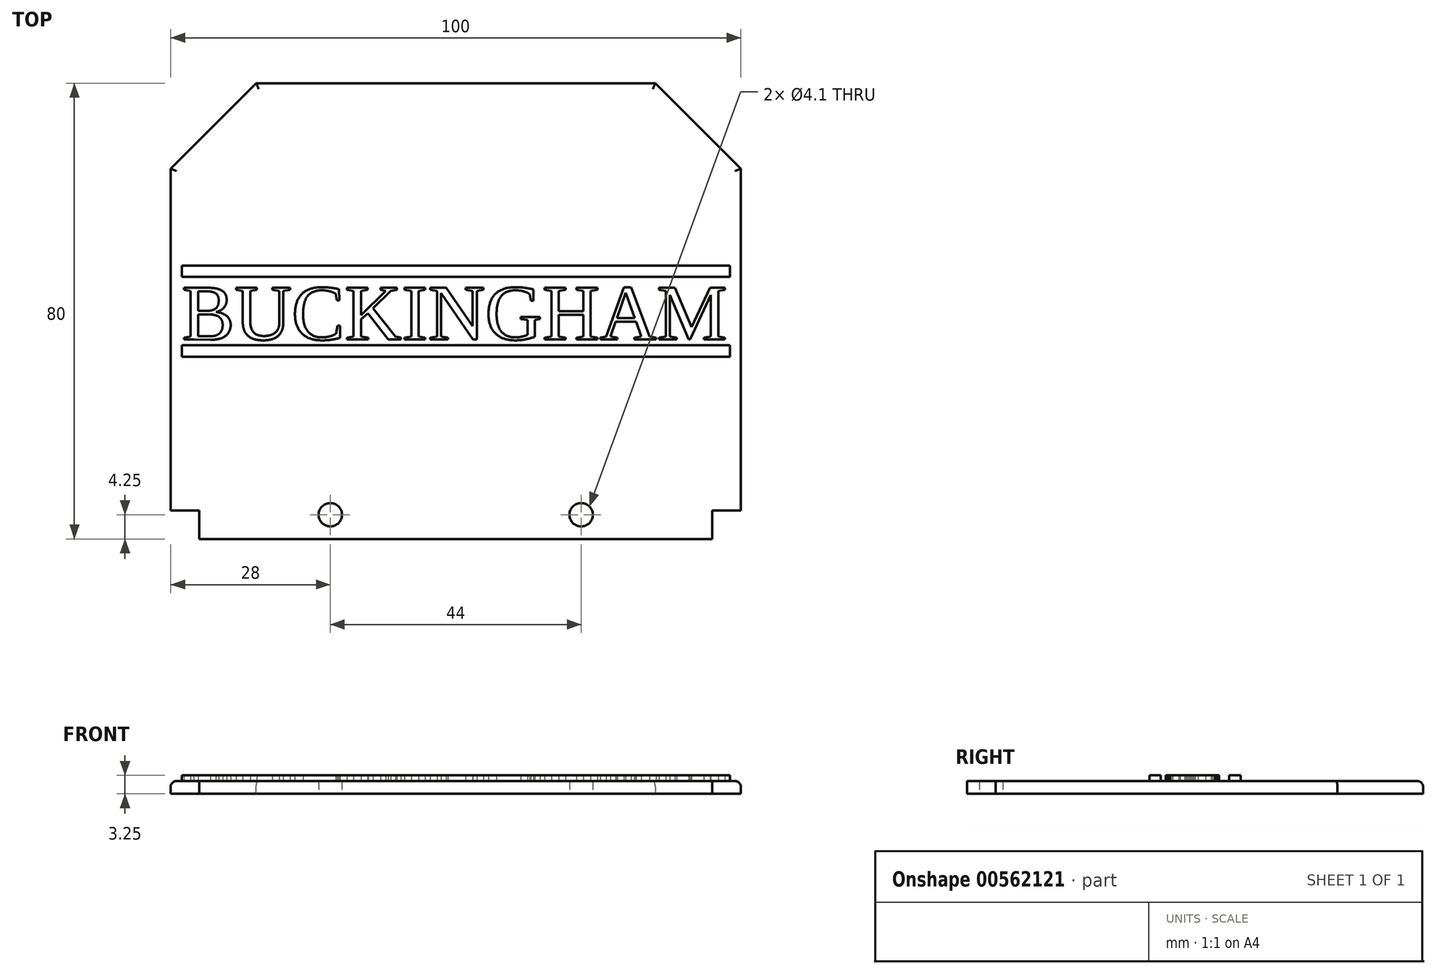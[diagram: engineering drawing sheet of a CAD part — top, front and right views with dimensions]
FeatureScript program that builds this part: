
annotation { "Feature Type Name" : "Feature", "Feature Type Description" : "" }
export const myFeature = defineFeature(function(context is Context, id is Id, definition is map)
    precondition{}
    {
        {
            var Q0;
            Q0=qCreatedBy(makeId("Top.planeOp"),FACE);
            var sketch = newSketch(context, id + "F0", { "sketchPlane" : qUnion([Q0])});
            skLineSegment(sketch, "E0.bottom", {"start": v(-50, -40) * mm, "end": v(50, -40) * mm});
            skLineSegment(sketch, "E0.top", {"start": v(-50, 40) * mm, "end": v(50, 40) * mm});
            skLineSegment(sketch, "E0.left", {"start": v(-50, -40) * mm, "end": v(-50, 40) * mm});
            skLineSegment(sketch, "E0.right", {"start": v(50, -40) * mm, "end": v(50, 40) * mm});
            skPoint(sketch, "E0.middle", {"position": v(0, 0) * mm});
            skPoint(sketch, "E1", {"position": v(0, -40) * mm});
            skLineSegment(sketch, "E2", {"start": v(-22, -35.75) * mm, "end": v(22, -35.75) * mm, "construction": true});
            skPoint(sketch, "E3", {"position": v(0, -35.75) * mm});
            skLineSegment(sketch, "E4", {"start": v(0, -40) * mm, "end": v(0, -35.75) * mm, "construction": true});
            skCircle(sketch, "E5", {"center": v(-22, -35.75) * mm, "radius": 2.05 * mm});
            skCircle(sketch, "E6.MirrorC", {"center": v(22, -35.75) * mm, "radius": 2.05 * mm});
            skLineSegment(sketch, "E7", {"start": v(-45, -40) * mm, "end": v(45, -40) * mm, "construction": true});
            skLineSegment(sketch, "E8.bottom", {"start": v(-45, -40) * mm, "end": v(-50, -40) * mm});
            skLineSegment(sketch, "E8.top", {"start": v(-45, -35) * mm, "end": v(-50, -35) * mm});
            skLineSegment(sketch, "E8.left", {"start": v(-45, -40) * mm, "end": v(-45, -35) * mm});
            skLineSegment(sketch, "E8.right", {"start": v(-50, -40) * mm, "end": v(-50, -35) * mm});
            skLineSegment(sketch, "E9.MirrorCS", {"start": v(45, -40) * mm, "end": v(45, -35) * mm});
            skLineSegment(sketch, "E10.MirrorCS", {"start": v(45, -35) * mm, "end": v(50, -35) * mm});
            skSolve(sketch);
        }
        {
            var Q0;
            {var subQ0=sQuery(id+"F0.wireOp",EDGE,"E0.top");Q0=makeQuery(id+"F0.imprint","IMPRINT",FACE,{"disambiguationData":[TD([[makeQuery(id+"F0.imprint","IMPRINT",EDGE,{"derivedFrom":subQ0}),-1.0]])]});}
            extrude(context, id + "F1", {"entities" : qUnion([Q0]), "depth" : 2.25 * mm, "offsetDistance" : 25 * mm});
        }
        {
            var Q0;
            Q0=makeQuery(id+"F1.opExtrude","CAP_FACE",FACE,{"disambiguationData":[OSD([sQuery(id+"F0.wireOp",EDGE,"E0.bottom"),sQuery(id+"F0.wireOp",EDGE,"E0.top"),sQuery(id+"F0.wireOp",EDGE,"E0.left"),sQuery(id+"F0.wireOp",EDGE,"E0.right"),sQuery(id+"F0.wireOp",EDGE,"E5"),sQuery(id+"F0.wireOp",EDGE,"E6.MirrorC")])],"isStart":false});
            var sketch = newSketch(context, id + "F2", { "sketchPlane" : qUnion([Q0])});
            skLineSegment(sketch, "E11", {"start": v(0, 0) * mm, "end": v(0, 5) * mm, "construction": true});
            skLineSegment(sketch, "E12", {"start": v(0, 5) * mm, "end": v(-48.07, 5) * mm, "construction": true});
            skText(sketch, "E13", { "text": "BUCKINGHAM", "fontName": "Tinos-Regular.ttf"});
            skLineSegment(sketch, "E14", {"start": v(0, 0) * mm, "end": v(0, -7) * mm, "construction": true});
            skLineSegment(sketch, "E15.bottom", {"start": v(-48.07, -6) * mm, "end": v(48.07, -6) * mm});
            skLineSegment(sketch, "E15.top", {"start": v(-48.07, -8) * mm, "end": v(48.07, -8) * mm});
            skLineSegment(sketch, "E15.left", {"start": v(-48.07, -6) * mm, "end": v(-48.07, -8) * mm});
            skLineSegment(sketch, "E15.right", {"start": v(48.07, -6) * mm, "end": v(48.07, -8) * mm});
            skPoint(sketch, "E15.middle", {"position": v(0, -7) * mm});
            skLineSegment(sketch, "E16", {"start": v(0, 0) * mm, "end": v(-50, 0) * mm, "construction": true});
            skLineSegment(sketch, "E17.MirrorCS", {"start": v(-48.07, 6) * mm, "end": v(48.07, 6) * mm});
            skLineSegment(sketch, "E18.MirrorCS", {"start": v(-48.07, 8) * mm, "end": v(48.07, 8) * mm});
            skLineSegment(sketch, "E19.MirrorCS", {"start": v(-48.07, 6) * mm, "end": v(-48.07, 8) * mm});
            skLineSegment(sketch, "E20.MirrorCS", {"start": v(48.07, 6) * mm, "end": v(48.07, 8) * mm});
            const initialGuessF2  = {"E13": [-0.04807, -0.005, 1, 0, 0.01]};
            skSetInitialGuess(sketch, initialGuessF2);
            skSolve(sketch);
        }
        {
            var Q0;
            Q0 = qSketchRegion(id + "F2", true);
            extrude(context, id + "F3", {"entities" : qUnion([Q0]), "operationType" : NewBodyOperationType.ADD, "depth" : 1 * mm, "offsetDistance" : 25 * mm});
        }
        {
            var Q0;
            Q0=makeQuery(id+"F1.opExtrude","SWEPT_EDGE",EDGE,{"disambiguationData":[OSD([sQuery(id+"F0.wireOp",EDGE,"E0.top"),sQuery(id+"F0.wireOp",EDGE,"E0.left")])]});
            var Q1;
            Q1=makeQuery(id+"F1.opExtrude","SWEPT_EDGE",EDGE,{"disambiguationData":[OSD([sQuery(id+"F0.wireOp",EDGE,"E0.top"),sQuery(id+"F0.wireOp",EDGE,"E0.right")])]});
            chamfer(context, id + "F4", {"entities" : qUnion([Q0, Q1]), "width" : 15 * mm, "tangentPropagation" : true});
        }
        {
            var Q0;
            Q0=makeQuery(id+"F1.opExtrude","CAP_EDGE",EDGE,{"disambiguationData":[OSD([sQuery(id+"F0.wireOp",EDGE,"E0.top")])],"isStart":false});
            var Q1;
            {var subQ0=sQuery(id+"F0.wireOp",EDGE,"E0.bottom");var subQ1=sQuery(id+"F0.wireOp",EDGE,"E6.MirrorC");var subQ2=sQuery(id+"F0.wireOp",EDGE,"E5");var subQ3=sQuery(id+"F0.wireOp",EDGE,"E0.right");var subQ4=sQuery(id+"F0.wireOp",EDGE,"E0.top");var subQ5=sQuery(id+"F0.wireOp",EDGE,"E0.left");Q1=makeQuery(id+"F4.opChamfer","BLEND_EDGE",EDGE,{"blendedFrom":[makeQuery(id+"F1.opExtrude","SWEPT_EDGE",EDGE,{"disambiguationData":[OSD([subQ4,subQ5])]}),makeQuery(id+"F3.boolean.opBoolean","SPLIT",FACE,{"disambiguationData":[TD([makeQuery(id+"F1.opExtrude","SWEPT_FACE",FACE,{"disambiguationData":[OSD([subQ0])]})])],"derivedFrom":makeQuery(id+"F1.opExtrude","CAP_FACE",FACE,{"disambiguationData":[OSD([subQ0,subQ4,subQ5,subQ3,subQ2,subQ1])],"isStart":false})})],"blendedInto":[makeQuery(id+"F3.boolean.opBoolean","SPLIT",FACE,{"disambiguationData":[TD([makeQuery(id+"F1.opExtrude","SWEPT_FACE",FACE,{"disambiguationData":[OSD([subQ0])]})])],"derivedFrom":makeQuery(id+"F1.opExtrude","CAP_FACE",FACE,{"disambiguationData":[OSD([subQ0,subQ4,subQ5,subQ3,subQ2,subQ1])],"isStart":false})})]});}
            var Q2;
            Q2=makeQuery(id+"F1.opExtrude","CAP_EDGE",EDGE,{"disambiguationData":[OSD([sQuery(id+"F0.wireOp",EDGE,"E0.left")])],"isStart":false});
            var Q3;
            {var subQ0=sQuery(id+"F0.wireOp",EDGE,"E0.bottom");var subQ1=sQuery(id+"F0.wireOp",EDGE,"E6.MirrorC");var subQ2=sQuery(id+"F0.wireOp",EDGE,"E5");var subQ3=sQuery(id+"F0.wireOp",EDGE,"E0.right");var subQ4=sQuery(id+"F0.wireOp",EDGE,"E0.top");var subQ5=sQuery(id+"F0.wireOp",EDGE,"E0.left");Q3=makeQuery(id+"F4.opChamfer","BLEND_EDGE",EDGE,{"blendedFrom":[makeQuery(id+"F1.opExtrude","SWEPT_EDGE",EDGE,{"disambiguationData":[OSD([subQ4,subQ3])]}),makeQuery(id+"F3.boolean.opBoolean","SPLIT",FACE,{"disambiguationData":[TD([makeQuery(id+"F1.opExtrude","SWEPT_FACE",FACE,{"disambiguationData":[OSD([subQ0])]})])],"derivedFrom":makeQuery(id+"F1.opExtrude","CAP_FACE",FACE,{"disambiguationData":[OSD([subQ0,subQ4,subQ5,subQ3,subQ2,subQ1])],"isStart":false})})],"blendedInto":[makeQuery(id+"F3.boolean.opBoolean","SPLIT",FACE,{"disambiguationData":[TD([makeQuery(id+"F1.opExtrude","SWEPT_FACE",FACE,{"disambiguationData":[OSD([subQ0])]})])],"derivedFrom":makeQuery(id+"F1.opExtrude","CAP_FACE",FACE,{"disambiguationData":[OSD([subQ0,subQ4,subQ5,subQ3,subQ2,subQ1])],"isStart":false})})]});}
            var Q4;
            Q4=makeQuery(id+"F1.opExtrude","CAP_EDGE",EDGE,{"disambiguationData":[OSD([sQuery(id+"F0.wireOp",EDGE,"E0.right")])],"isStart":false});
            fillet(context, id + "F5", {"entities" : qUnion([Q0, Q1, Q2, Q3, Q4]), "radius" : 1 * mm, "tangentPropagation" : true, "allowEdgeOverflow" : false});
        }
    });
